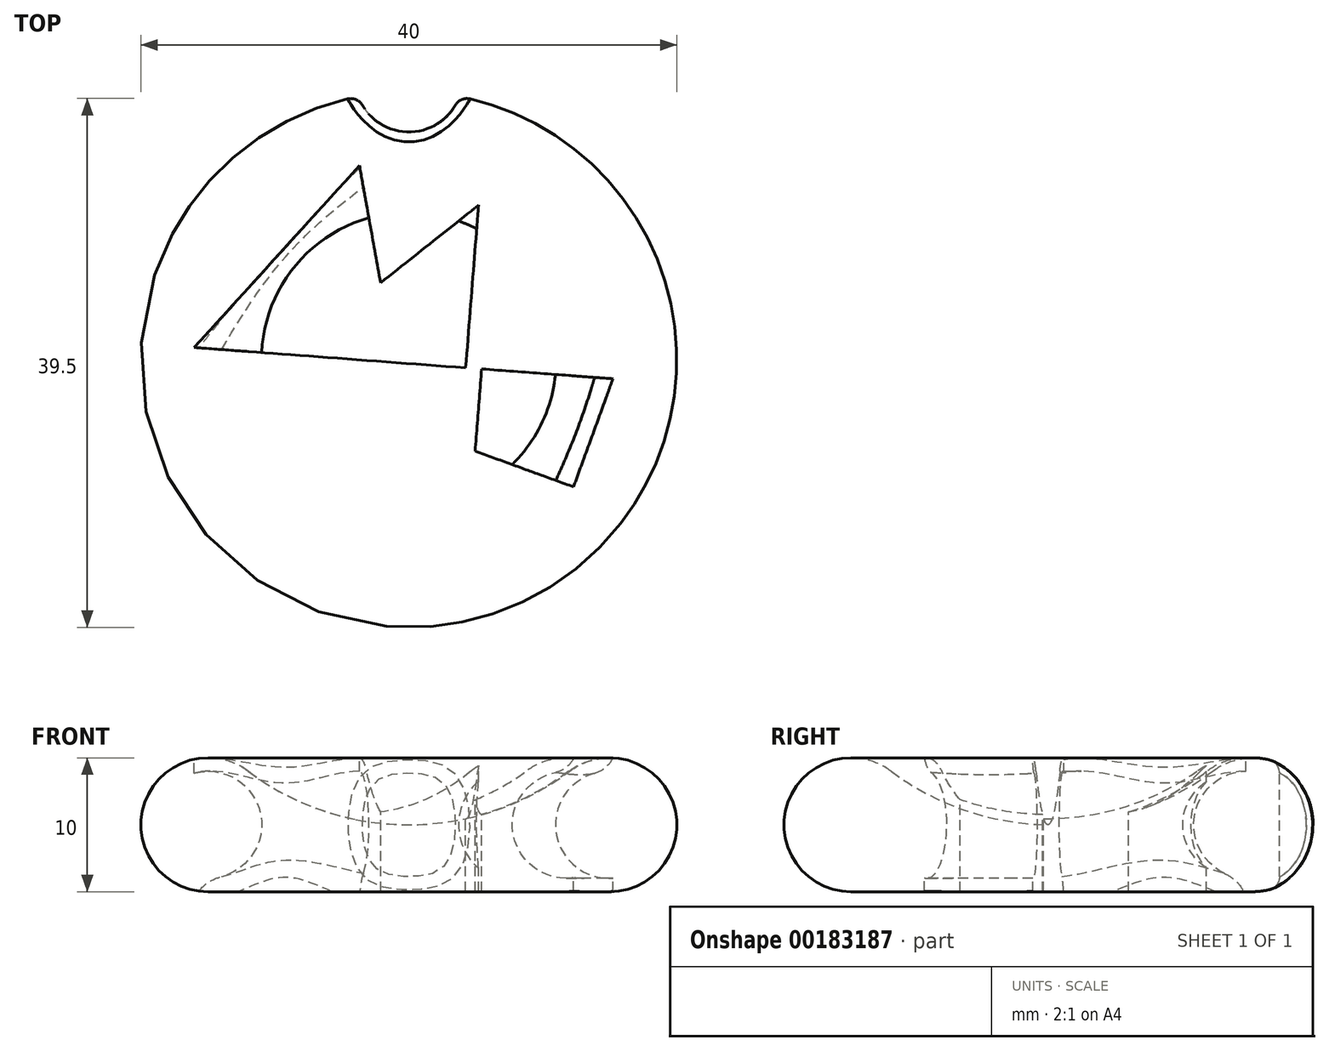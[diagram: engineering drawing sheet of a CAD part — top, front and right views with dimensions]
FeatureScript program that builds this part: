
annotation { "Feature Type Name" : "Feature", "Feature Type Description" : "" }
export const myFeature = defineFeature(function(context is Context, id is Id, definition is map)
    precondition{}
    {
        {
            var Q0;
            Q0=qCreatedBy(makeId("Front.planeOp"),FACE);
            var sketch = newSketch(context, id + "F0", { "sketchPlane" : qUnion([Q0])});
            skArc(sketch, "E0", {"start": v(-12, 4) * mm, "mid": v(-19.74, 1.58) * mm, "end": v(-15, -5) * mm});
            skArc(sketch, "E1", {"start": v(-12, 4) * mm, "mid": v(-6.32, 1.03) * mm, "end": v(0, 0) * mm});
            skLineSegment(sketch, "E2", {"start": v(-15, -5) * mm, "end": v(0, -5) * mm});
            skLineSegment(sketch, "E3", {"start": v(0, -5) * mm, "end": v(0, 0) * mm});
            skSolve(sketch);
        }
        {
            var Q0;
            Q0=makeQuery(id+"F0.imprint","IMPRINT",FACE,{"disambiguationData":[TD([[makeQuery(id+"F0.imprint","IMPRINT",EDGE,{"derivedFrom":sQuery(id+"F0.wireOp",EDGE,"E0")}),1.0]])]});
            var Q1;
            Q1=sQuery(id+"F0.wireOp",EDGE,"E3");
            revolve(context, id + "F1", {"entities" : qUnion([Q0]), "axis" : qUnion([Q1]), "revolveType" : RevolveType.FULL});
        }
        {
            var Q0;
            Q0=qCreatedBy(makeId("Top.planeOp"),FACE);
            cPlane(context, id + "F2", {"entities" : qUnion([Q0]), "cplaneType" : CPlaneType.OFFSET, "offset" : 5 * mm, "width" : 150 * mm, "height" : 150 * mm});
        }
        {
            var Q0;
            Q0=qCreatedBy(id+"F2.planeOp",FACE);
            var sketch = newSketch(context, id + "F3", { "sketchPlane" : qUnion([Q0])});
            skLineSegment(sketch, "E4", {"start": v(5.2, 11.54) * mm, "end": v(-2.11, 5.73) * mm});
            skLineSegment(sketch, "E5", {"start": v(-2.11, 5.73) * mm, "end": v(-3.69, 14.49) * mm});
            skLineSegment(sketch, "E6", {"start": v(-3.69, 14.49) * mm, "end": v(-16.02, 0.9) * mm});
            skLineSegment(sketch, "E7", {"start": v(-16.02, 0.9) * mm, "end": v(4.24, -0.61) * mm});
            skLineSegment(sketch, "E8", {"start": v(4.24, -0.61) * mm, "end": v(5.2, 11.54) * mm});
            skLineSegment(sketch, "E9", {"start": v(4.95, -6.84) * mm, "end": v(12.3, -9.51) * mm});
            skLineSegment(sketch, "E10", {"start": v(12.3, -9.51) * mm, "end": v(15.23, -1.43) * mm});
            skLineSegment(sketch, "E11", {"start": v(15.23, -1.43) * mm, "end": v(5.43, -0.7) * mm});
            skLineSegment(sketch, "E12", {"start": v(5.43, -0.7) * mm, "end": v(4.95, -6.84) * mm});
            skSolve(sketch);
        }
        {
            var Q0;
            Q0=qSketchRegion(id+"F3",true);
            var Q1;
            Q1=makeQuery(id+"F1.opRevolve","SWEPT_FACE",FACE,{"disambiguationData":[OSD([sQuery(id+"F0.wireOp",EDGE,"E0")])]});
            extrude(context, id + "F4", {"entities" : qUnion([Q0]), "operationType" : NewBodyOperationType.REMOVE, "oppositeDirection" : true, "endBoundEntityFace" : qUnion([Q1]), "depth" : 25 * mm});
        }
        {
            var Q0;
            Q0=qCreatedBy(makeId("Front.planeOp"),FACE);
            var sketch = newSketch(context, id + "F5", { "sketchPlane" : qUnion([Q0])});
            skCircle(sketch, "E13", {"center": v(-15, 0) * mm, "radius": 5 * mm, "construction": true});
            skCircle(sketch, "E14.0", {"center": v(-15, 0) * mm, "radius": 4 * mm});
            skSolve(sketch);
        }
        {
            var Q0;
            Q0=qSketchRegion(id+"F5",true);
            var Q1;
            Q1=sQuery(id+"F0.wireOp",EDGE,"E3");
            revolve(context, id + "F6", {"operationType" : NewBodyOperationType.ADD, "entities" : qUnion([Q0]), "axis" : qUnion([Q1]), "revolveType" : RevolveType.FULL});
        }
        {
            var Q0;
            Q0=qCreatedBy(makeId("Top.planeOp"),FACE);
            var sketch = newSketch(context, id + "F7", { "sketchPlane" : qUnion([Q0])});
            skCircle(sketch, "E15", {"center": v(0, 21) * mm, "radius": 4 * mm});
            skCircle(sketch, "E16", {"center": v(0, 0) * mm, "radius": 20 * mm, "construction": true});
            skSolve(sketch);
        }
        {
            var Q0;
            Q0=qSketchRegion(id+"F7",true);
            extrude(context, id + "F8", {"entities" : qUnion([Q0]), "operationType" : NewBodyOperationType.REMOVE, "endBound" : BoundingType.THROUGH_ALL, "oppositeDirection" : true, "depth" : 25 * mm, "hasSecondDirection" : true, "secondDirectionBound" : SecondDirectionBoundingType.THROUGH_ALL, "secondDirectionOppositeDirection" : false, "secondDirectionDepth" : 25 * mm});
        }
        {
            var Q0;
            Q0=makeQuery(id+"F8.boolean.opBoolean","INTERSECT",EDGE,{"derivedFrom":[makeQuery(id+"F1.opRevolve","SWEPT_FACE",FACE,{"disambiguationData":[OSD([sQuery(id+"F0.wireOp",EDGE,"E0")])]}),makeQuery(id+"F8.opExtrude","SWEPT_FACE",FACE,{"disambiguationData":[OSD([sQuery(id+"F7.wireOp",EDGE,"E15")])]})]});
            fillet(context, id + "F9", {"entities" : qUnion([Q0]), "radius" : 1 * mm, "tangentPropagation" : true, "allowEdgeOverflow" : false});
        }
        {
            var Q0;
            Q0=makeQuery(id+"F6.boolean.opBoolean","INTERSECT",EDGE,{"disambiguationData":[OD(0.0)],"derivedFrom":[makeQuery(id+"F4.boolean.opBoolean","COPY",FACE,{"derivedFrom":makeQuery(id+"F4.opExtrude","SWEPT_FACE",FACE,{"disambiguationData":[OSD([sQuery(id+"F3.wireOp",EDGE,"E6")])]})}),makeQuery(id+"F6.opRevolve","SWEPT_FACE",FACE,{"disambiguationData":[OSD([sQuery(id+"F5.wireOp",EDGE,"E14.0")])]})]});
            var Q1;
            Q1=makeQuery(id+"F6.boolean.opBoolean","INTERSECT",EDGE,{"disambiguationData":[OD(1.0)],"derivedFrom":[makeQuery(id+"F4.boolean.opBoolean","COPY",FACE,{"derivedFrom":makeQuery(id+"F4.opExtrude","SWEPT_FACE",FACE,{"disambiguationData":[OSD([sQuery(id+"F3.wireOp",EDGE,"E10")])]})}),makeQuery(id+"F6.opRevolve","SWEPT_FACE",FACE,{"disambiguationData":[OSD([sQuery(id+"F5.wireOp",EDGE,"E14.0")])]})]});
            fillet(context, id + "F10", {"entities" : qUnion([Q0, Q1]), "radius" : 2 * mm, "tangentPropagation" : true, "allowEdgeOverflow" : false});
        }
    });
